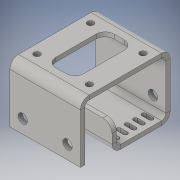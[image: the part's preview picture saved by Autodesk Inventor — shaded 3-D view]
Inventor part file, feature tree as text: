
AUTODESK INVENTOR PART (.ipt)
format: ipt  version: 2016 (Build 200138000, 138)  size: 278,016 bytes
history: native  units: in
note: dims shown in document units (in); Inventor stores cm internally (conversion verified against a paired STEP export)
features: sheet_metal_op x8, sketch x5, other x5, plane x2, mirror x2, chamfer x2, pattern_linear x2, projected_geometry x2
ambient origin geometry x8: Origin, YZ Plane, XZ Plane, XY Plane, X Axis, Y Axis, Z Axis, Center Point
bodies: Body1 (feature_tree)
feature tree (28):
  sheet_metal_op  "Face1"
  plane  "Work Plane2"
  mirror  "Mirror1"
  sheet_metal_op  "Bend1"
  sheet_metal_op  "Flange1"
  sheet_metal_op  "Flange2"
  chamfer  "Corner Round1"
  pattern_linear  "Rectangular Pattern1"  Spacing1=0.12in  [1 undecoded]
  pattern_linear  "Rectangular Pattern2"  Spacing1=0.06in  [1 undecoded]
  plane  "Work Plane3"
  mirror  "Mirror2"
  chamfer  "Corner Round2"
  sketch  "Sketch5"  dims[d1=0.2598in]
  other  "Plate1"
  sketch  "Sketch7"  dims[d2=0.2598in]
  other  "Plate2"
  sheet_metal_op  "Bend2"
  sheet_metal_op  "Corner1"
  sketch  "Sketch8"  dims[d3=1.25in]
  other  "Plate3"
  sheet_metal_op  "Bend3"
  sheet_metal_op  "Corner2"
  sketch  "Sketch9"  dims[d6=0.12in]
  projected_geometry  "Projected Loop1"
  sketch  "Sketch10"  dims[d7=-1.25in d8=0.12in d9=0.06in d10=0.24in d11=0.12in d12=0.12in d13=0.12in d14=0.06in d15=0.24in d16=0.12in d17=1.5in d18=90.0deg d19=0.12in d20=0.48in d21=0.12in d22=0.12in d23=0.12in d24=0.06in d25=0.24in d26=0.12in d27=0.75in d28=90.0deg d29=0.12in d30=0.48in d31=0.12in d32=0.12in d33=0.25in d34=0.1969in d35=0.1181in d36=0.1969in d37=0.12in d38=0.0in d39=1.1811in d41=0.2362in d42=1.1811in d44=-0.2362in d45=0.1969in d46=0.1969in d47=0.5906in d48=0.5906in d49=0.1732in d50=0.12in d51=0.0in d52=0.25in]
  projected_geometry  "Projected Loop2"
  other  "Cut1"
  other  "Cut2"
note: 2 required parameter values undecoded (feature->parameter linkage not recoverable at this tier; creation-order binding heuristic only, values carry confidence <= 0.55)
